# Revit family: Loudspeaker_Bose_ArenaMatch-AMU108_with-Pan-and-Tilt-Bracket_1
name_source: partatom
category: Communication Devices
revit_build: Autodesk Revit 2015 (Build: 20160512_0715(x64)
units: mm (PartAtom-declared; Revit-internal decimal feet)

## types (2) — shared parameters
Crossover = Passive (1.4 kHz crossover frequeuncy)
Default Elevation = 1219 mm
Depth = 279 mm
Description = Bose Professional ArenaMatch loudspeakers bring proven DeltaQ sound quality and flexibility to outdoor installations — sports stadiums, arenas, outdoor entertainment centers, and more.
Edition number = 1
Enviromental = IEC 60529 IP55 for outdoor, direct-exposure installations
Frequency Range = 80 Hz to 18 kHz
Frequency Response = 90 Hz to 16 kHz
HF Driver = 1 × Bose EMB2S extended high-frequency compression driver (2-inch voice coil)
Height = 236 mm
LF Driver = 1 × Bose LF8 high-excursion 8-inch woofer (2-inch voice coil)
Manufacturer = Bose Professional
Mounting/Suspension = 2x M8 threaded inserts for U-bracket; 4x M8 threaded inserts on rear (127 × 70 mm, 4-bolt pattern)
Nominal Coverage Pattern = 90° × 60°
Nominal Impedance = 8 Ω
Nominal Sensitivity = Bose Extended Lifecycle Test: Free field - 91 dB, Wall/Ceilling - 93 dB; AES Transducer Test: Free field - 91 dB, Wall/Ceilling - 93 dB;
Power Connector = 1x barrier strip, (accepts 10 to 18 wire gauge)
Power Handling(Long-term continuous) = Bose Extended Lifecycle Test: 200W; AES Transducer Test: 250W
Power Handling(peak) = Bose Extended Lifecycle Test: 800W; AES Transducer Test: 1000W
Product Guid = 6cfa4dc9-d9f0-4af4-b6e5-06893246b780
Product data url = https://bimobject.com
Rated Maximum SPL = Calculated max. SPL @ 1 m (Bose power test) -  Free field: 91 dB, Wall/Ceilling: 93 dB ; Calculated max. SPL @ 1 m (2-hour power test) - Free field: 91 dB, Wall/Ceilling: 93 dB; Calculated max. SPL @ 1 m (Bose power test), peak - Free field: 120 dB, Wall/Ceilling: 122 dB; Calculated max. SPL @ 1 m (2-hour power test),
peak -Free field: 121 dB, Wall/Ceilling: 123 dB;
Recommended High-pass Filter = 80 Hz with minimum 12-dB / octave filter
Transformer Taps Information = 70V: 5, 10, 20, 40, 80 W; 100V: 10, 20, 40, 80 W
URL = https://pro.bose.com
Weight = 10.57 kg
Width = 470 mm

## per-type parameters (varying)
| type | Bracket Material | Grill Material | Product code | Speaker Material |
| 811433-0110 Black | Metal-Bose-Black | Grill-Bose-Black | 811434-0110 | Matt-Bose-Black |
| 811433-0210 White | Metal-Bose-White | Grill-Bose-White | 811434-0210 | Matt-Bose-White |

note: column(s) folded — value = type name in every type: Model

## geometry (parser evidence)
native form markers: Blend x4, Sweep x8
no freeform markers — native parametric forms only
